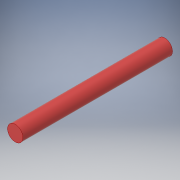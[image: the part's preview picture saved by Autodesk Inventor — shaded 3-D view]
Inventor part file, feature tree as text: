
AUTODESK INVENTOR PART (.ipt)
format: ipt  version: 2019 (Build 230136000, 136)  size: 92,160 bytes
history: native  units: mm
features: extrude x1, sketch x1
ambient origin geometry x8: Origin, YZ Plane, XZ Plane, XY Plane, X Axis, Y Axis, Z Axis, Center Point
bodies: Solid1 (feature_tree)
feature tree (2):
  extrude  "Extrusion1"  Depth=34.0mm TaperAngle=0.0deg
  sketch  "Sketch1"  dims[d0=3.5mm d1=34.0mm d2=0.0mm]
